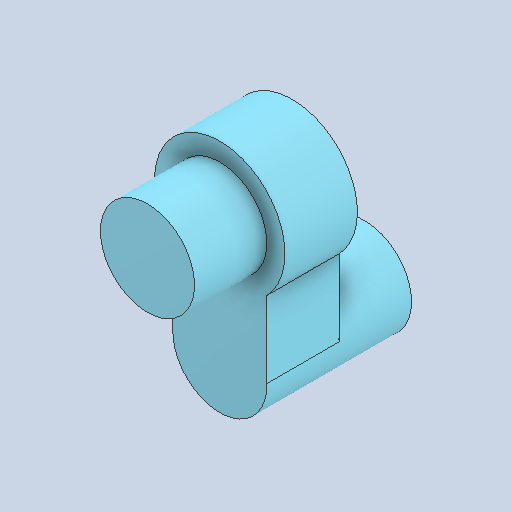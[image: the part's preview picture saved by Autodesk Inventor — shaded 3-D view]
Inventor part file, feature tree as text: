
AUTODESK INVENTOR PART (.ipt)
format: ipt  version: 2022 (Build 260153000, 153)  size: 134,144 bytes
history: native  units: in
note: dims shown in document units (in); Inventor stores cm internally (conversion verified against a paired STEP export)
features: other x3, sketch x2
ambient origin geometry x8: Origin, YZ Plane, XZ Plane, XY Plane, X Axis, Y Axis, Z Axis, Center Point
bodies: Solid1 (feature_tree)
feature tree (5):
  other  "Component37.ipt"
  other  "Solid1::Component37.ipt"
  other  "TaggingFeature1"
  sketch  "Sketch2"  dims[d0=0.3937in]
  sketch  "Sketch3"
